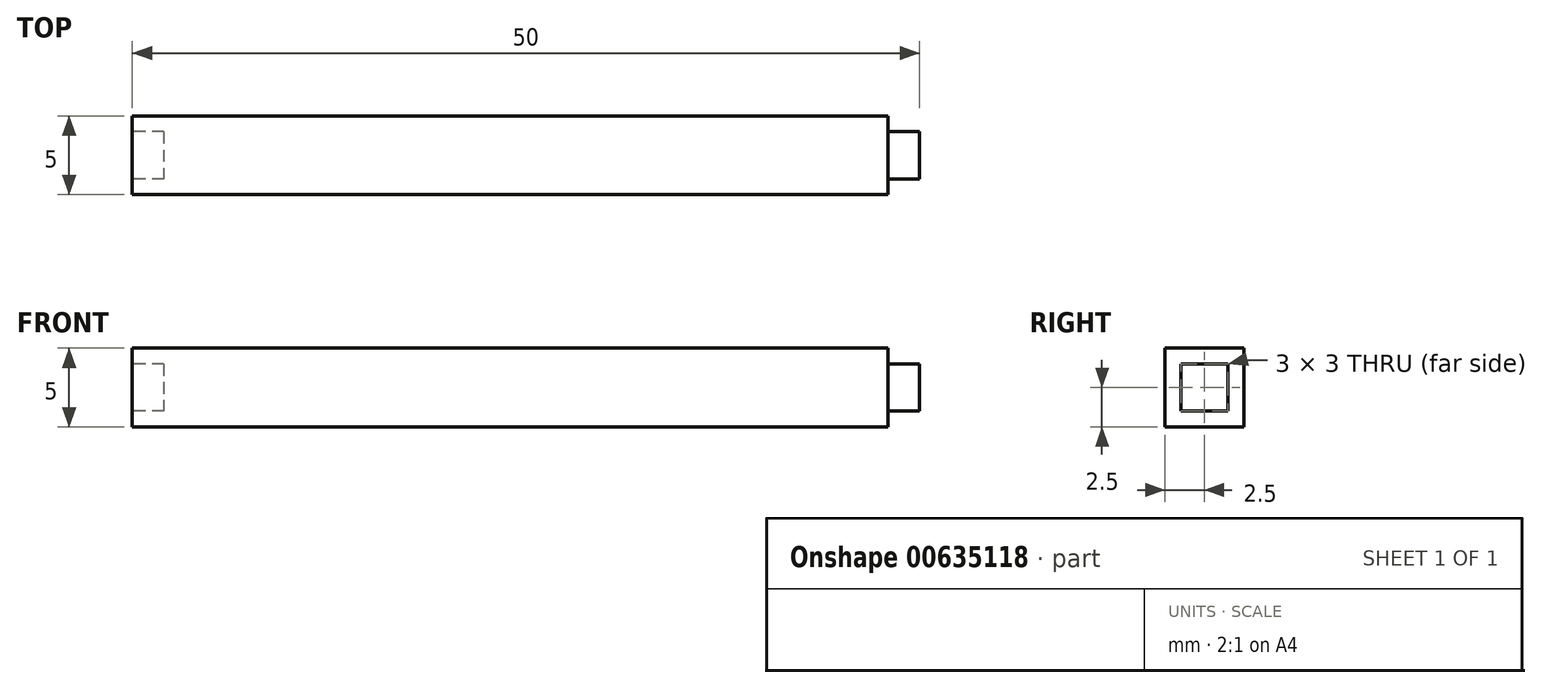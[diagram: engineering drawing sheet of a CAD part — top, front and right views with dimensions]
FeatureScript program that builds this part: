
annotation { "Feature Type Name" : "Feature", "Feature Type Description" : "" }
export const myFeature = defineFeature(function(context is Context, id is Id, definition is map)
    precondition{}
    {
        {
            var Q0;
            Q0=qCreatedBy(makeId("Front.planeOp"),FACE);
            var sketch = newSketch(context, id + "F0", { "sketchPlane" : qUnion([Q0])});
            skLineSegment(sketch, "E0.bottom", {"start": v(-25, -2.5) * mm, "end": v(25, -2.5) * mm});
            skLineSegment(sketch, "E0.top", {"start": v(-25, 2.5) * mm, "end": v(25, 2.5) * mm});
            skLineSegment(sketch, "E0.left", {"start": v(-25, -2.5) * mm, "end": v(-25, 2.5) * mm});
            skLineSegment(sketch, "E0.right", {"start": v(25, -2.5) * mm, "end": v(25, 2.5) * mm});
            skPoint(sketch, "E0.middle", {"position": v(0, 0) * mm});
            skSolve(sketch);
        }
        {
            var Q0;
            Q0 = qSketchRegion(id + "F0", true);
            extrude(context, id + "F1", {"entities" : qUnion([Q0]), "depth" : 5 * mm, "offsetDistance" : 25.4 * mm});
        }
        {
            var Q0;
            Q0=makeQuery(id+"F1.opExtrude","SWEPT_FACE",FACE,{"disambiguationData":[OSD([sQuery(id+"F0.wireOp",EDGE,"E0.left")])]});
            var sketch = newSketch(context, id + "F2", { "sketchPlane" : qUnion([Q0])});
            skLineSegment(sketch, "E1.bottom", {"start": v(1, 1.5) * mm, "end": v(4, 1.5) * mm});
            skLineSegment(sketch, "E1.top", {"start": v(1, -1.5) * mm, "end": v(4, -1.5) * mm});
            skLineSegment(sketch, "E1.left", {"start": v(1, 1.5) * mm, "end": v(1, -1.5) * mm});
            skLineSegment(sketch, "E1.right", {"start": v(4, 1.5) * mm, "end": v(4, -1.5) * mm});
            skPoint(sketch, "E1.middle", {"position": v(2.5, 0) * mm});
            skPoint(sketch, "E1.middle.positionSnap0", {"position": v(2.5, 2.5) * mm});
            skPoint(sketch, "E1.middle.positionSnap1", {"position": v(0, 0) * mm});
            skPoint(sketch, "E1.centerSnap0", {"position": v(2.5, 2.5) * mm});
            skPoint(sketch, "E1.centerSnap1", {"position": v(0, 0) * mm});
            skSolve(sketch);
        }
        {
            var Q0;
            Q0 = qSketchRegion(id + "F2", true);
            extrude(context, id + "F3", {"entities" : qUnion([Q0]), "operationType" : NewBodyOperationType.REMOVE, "oppositeDirection" : true, "depth" : 2 * mm, "offsetDistance" : 25 * mm});
        }
        {
            var Q0;
            Q0=makeQuery(id+"F1.opExtrude","SWEPT_FACE",FACE,{"disambiguationData":[OSD([sQuery(id+"F0.wireOp",EDGE,"E0.right")])]});
            var sketch = newSketch(context, id + "F4", { "sketchPlane" : qUnion([Q0])});
            skLineSegment(sketch, "E2.bottom", {"start": v(-4, -1.5) * mm, "end": v(-1, -1.5) * mm});
            skLineSegment(sketch, "E2.top", {"start": v(-4, 1.5) * mm, "end": v(-1, 1.5) * mm});
            skLineSegment(sketch, "E2.left", {"start": v(-4, -1.5) * mm, "end": v(-4, 1.5) * mm});
            skLineSegment(sketch, "E2.right", {"start": v(-1, -1.5) * mm, "end": v(-1, 1.5) * mm});
            skPoint(sketch, "E2.middle", {"position": v(-2.5, 0) * mm});
            skPoint(sketch, "E2.middle.positionSnap0", {"position": v(-2.5, 2.5) * mm});
            skPoint(sketch, "E2.middle.positionSnap1", {"position": v(-5, 0) * mm});
            skPoint(sketch, "E2.centerSnap0", {"position": v(-2.5, 2.5) * mm});
            skPoint(sketch, "E2.centerSnap1", {"position": v(-5, 0) * mm});
            skSolve(sketch);
        }
        {
            var Q0;
            Q0=makeQuery(id+"F4.imprint","IMPRINT",FACE,{"disambiguationData":[TD([[makeQuery(id+"F4.imprint","IMPRINT",EDGE,{"derivedFrom":sQuery(id+"F4.wireOp",EDGE,"E2.bottom")}),-1.0]])]});
            extrude(context, id + "F5", {"entities" : qUnion([Q0]), "operationType" : NewBodyOperationType.REMOVE, "oppositeDirection" : true, "depth" : 2 * mm, "offsetDistance" : 25 * mm});
        }
    });
